# Revit family: HansWeitzel_52280
name_source: partatom
category: Allgemeines Modell
revit_build: Autodesk Revit 2017 (Build: 20160225_1515(x64)
units: mm (PartAtom-declared; Revit-internal decimal feet)

## family parameters
Arbeitsebenenbasiert = Nein
Beim Laden mit Abzugskörper schneiden = Nein
Bemaßung runder Anschluss = Durchmesser verwenden
Gemeinsam genutzt = Nein
Immer vertikal = Ja
Kann Basisbauteil für Bewehrung sein = Nein
Raumberechnungspunkt = Nein
Teiletyp = Normal

## types (1)
- HansWeitzel_52280
    BIM = https://media.live.bim.site
    BIMSITE_PRODUCT_ID = 3575323fc205efaadee0f21cb8608206c300e5b7
    Beschreibung = HZ-Teppichsockelleiste SLT Weiß, 2m mit Selbstklebeband f. Teppicheinlage
    Brandklasse B2 = Ja
    Breite [mm] = 2000
    Dekor = Weiß
    Farbton = weiß
    GTIN = 4022023111910
    Gewicht unverpackt (netto) [kg] = 0.86
    HAN = 52280
    HeinzeBIM = https://www.heinze.de
    Hersteller = Hans Weitzel GmbH & Co. KG
    Höhe [mm] = 96
    Ist System = Nein
    Ist Zubehör = Nein
    Length1 = 2000 mm
    Menge pro Verpackungseinheit = 10
    Profilart = Sockelprofil
    Selbstverlöschend = Ja
    Tiefe (mm) = 46
    Typname = HZ-Teppichsockelleiste SLT Weiß, 2m
    Wandmontage möglich = Ja
    Werkstoff = PVC
    max. Betriebstemperatur (°C) = 90

## geometry (parser evidence)
native form markers: Sweep x2
no freeform markers — native parametric forms only
